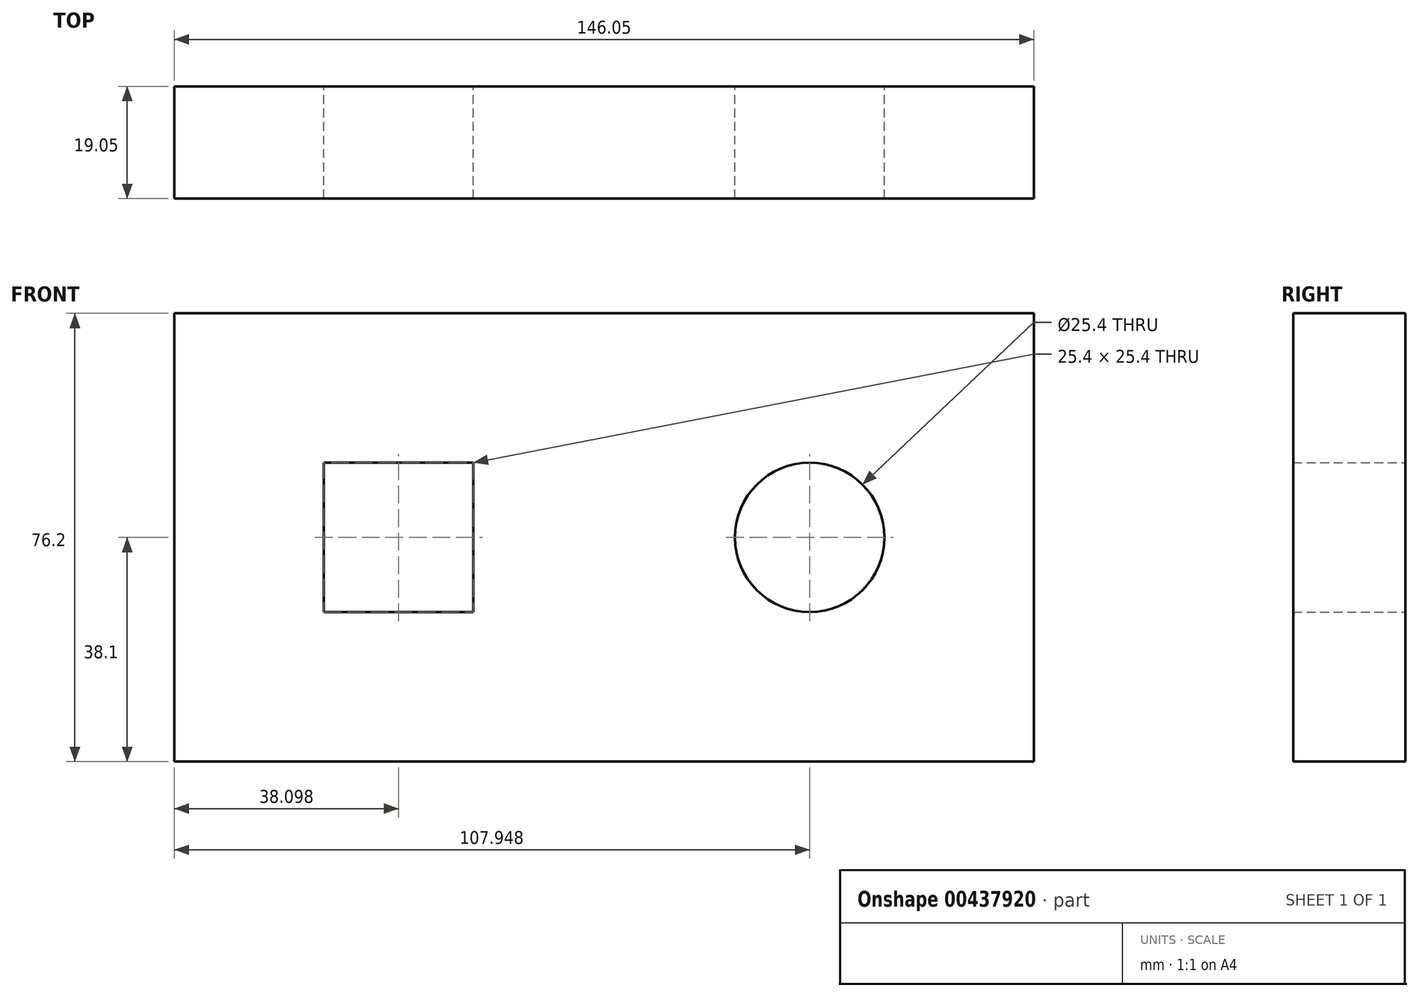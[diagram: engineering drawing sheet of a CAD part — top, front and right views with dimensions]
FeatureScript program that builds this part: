
annotation { "Feature Type Name" : "Feature", "Feature Type Description" : "" }
export const myFeature = defineFeature(function(context is Context, id is Id, definition is map)
    precondition{}
    {
        {
            var Q0;
            Q0=qCreatedBy(makeId("Front.planeOp"),FACE);
            var sketch = newSketch(context, id + "F0", { "sketchPlane" : qUnion([Q0])});
            skLineSegment(sketch, "E0", {"start": v(-76.38, 0) * mm, "end": v(69.67, 0) * mm});
            skLineSegment(sketch, "E1", {"start": v(69.67, 0) * mm, "end": v(69.67, 76.2) * mm});
            skLineSegment(sketch, "E2", {"start": v(69.67, 76.2) * mm, "end": v(-76.38, 76.2) * mm});
            skLineSegment(sketch, "E3", {"start": v(-76.38, 76.2) * mm, "end": v(-76.38, 0) * mm});
            skLineSegment(sketch, "E4.bottom", {"start": v(-50.98, 50.8) * mm, "end": v(-25.58, 50.8) * mm});
            skLineSegment(sketch, "E4.top", {"start": v(-50.98, 25.4) * mm, "end": v(-25.58, 25.4) * mm});
            skLineSegment(sketch, "E4.left", {"start": v(-50.98, 50.8) * mm, "end": v(-50.98, 25.4) * mm});
            skLineSegment(sketch, "E4.right", {"start": v(-25.58, 50.8) * mm, "end": v(-25.58, 25.4) * mm});
            skCircle(sketch, "E5", {"center": v(31.57, 38.1) * mm, "radius": 12.7 * mm});
            skSolve(sketch);
        }
        {
            var Q0;
            Q0 = qSketchRegion(id + "F0", true);
            extrude(context, id + "F1", {"entities" : qUnion([Q0]), "depth" : 19.05 * mm});
        }
    });
